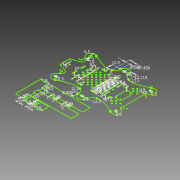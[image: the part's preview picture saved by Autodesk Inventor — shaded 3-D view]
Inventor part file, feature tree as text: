
AUTODESK INVENTOR PART (.ipt)
format: ipt  version: 2012 (Build 160160000, 160)  size: 219,648 bytes
history: native  units: mm
features: sketch x1
ambient origin geometry x8: Origin, YZ Plane, XZ Plane, XY Plane, X Axis, Y Axis, Z Axis, Center Point
feature tree (1):
  sketch  "Sketch1"  dims[d0=10.0mm d1=6.5mm d2=6.5mm d3=6.5mm d4=6.5mm d5=6.5mm d6=12.0mm d7=2.0mm d8=2.0mm d9=5.0mm d10=5.0mm d13=3.0mm d14=3.0mm d15=3.0mm d16=3.0mm d17=3.0mm d18=3.0mm d19=3.0mm d20=3.0mm d21=10.0mm d22=3.0mm d23=3.0mm d24=3.0mm d25=10.0mm d26=12.5mm d27=12.5mm d28=12.5mm d29=12.5mm d30=8.00764mm d31=17.45764mm d32=8.00764mm d33=12.118872mm d35=10.0mm d36=10.0mm d37=10.0mm d38=10.0mm d39=10.0mm d40=10.0mm d41=10.0mm d42=10.0mm d43=3.0mm d44=3.0mm d45=3.0mm d46=3.0mm d47=18.0mm d50=18.0mm d51=18.0mm d52=10.0mm d53=10.0mm d54=10.0mm d55=6.5mm d56=3.0mm d57=3.0mm d58=3.0mm d59=3.0mm d60=3.0mm d61=3.0mm d62=3.0mm d63=10.0mm d64=3.0mm d65=3.0mm d66=3.0mm d67=10.0mm d68=3.0mm d69=3.0mm d70=3.0mm d71=10.0mm d72=3.0mm d73=3.0mm d74=3.0mm d75=10.0mm d76=3.0mm d77=3.0mm d78=3.0mm d79=10.0mm d80=3.0mm d81=3.0mm d82=3.0mm d83=10.0mm d84=3.0mm d85=3.0mm d86=3.0mm d87=10.0mm d88=3.0mm d89=3.0mm d90=3.0mm d91=10.0mm d92=3.0mm d93=3.0mm d94=3.0mm d95=10.0mm d96=10.0mm d97=14.5mm d98=5.0mm d99=7.0mm d100=5.0mm d101=3.0mm d102=5.0mm d104=7.0mm d106=18.0mm d107=5.0mm d108=7.0mm d109=5.0mm d110=3.0mm d112=5.0mm d113=7.0mm]
